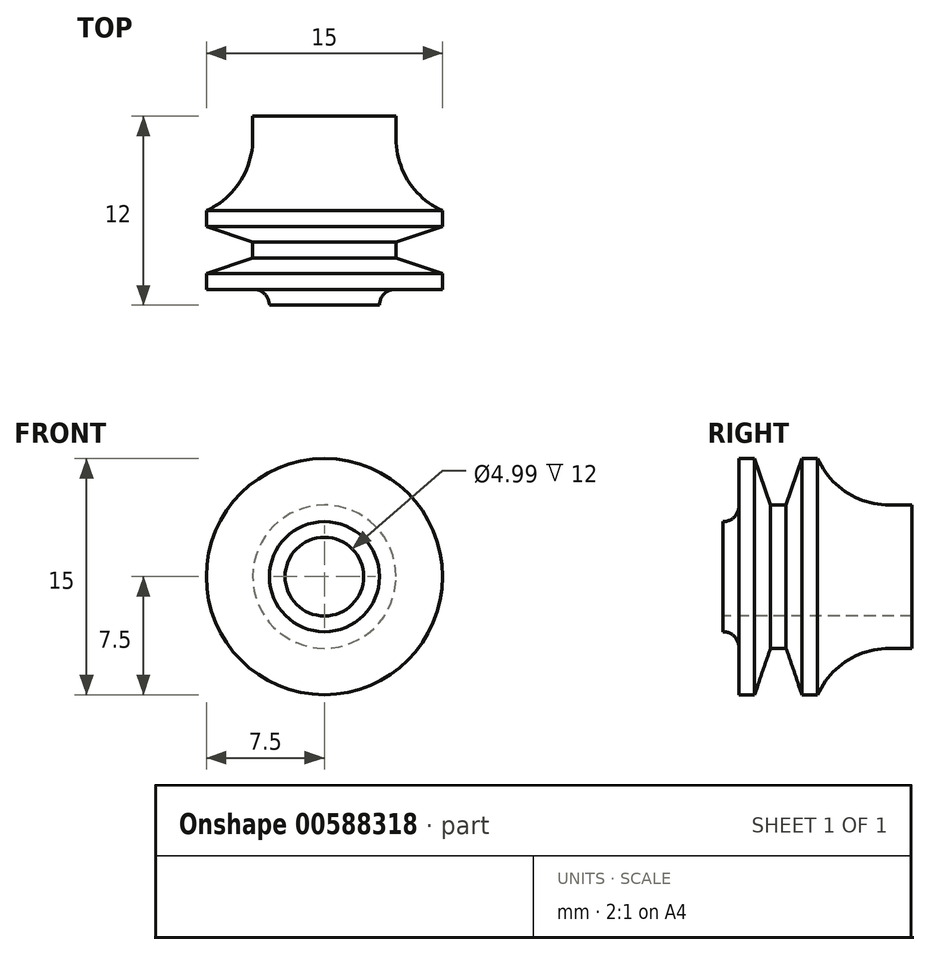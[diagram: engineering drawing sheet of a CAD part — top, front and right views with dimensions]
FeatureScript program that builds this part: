
annotation { "Feature Type Name" : "Feature", "Feature Type Description" : "" }
export const myFeature = defineFeature(function(context is Context, id is Id, definition is map)
    precondition{}
    {
        {
            var Q0;
            Q0=qCreatedBy(makeId("Right.planeOp"),FACE);
            var sketch = newSketch(context, id + "F0", { "sketchPlane" : qUnion([Q0])});
            skLineSegment(sketch, "E0", {"start": v(-124.9, 0) * mm, "end": v(95.35, 0) * mm, "construction": true});
            skLineSegment(sketch, "E1", {"start": v(-35.02, 89.98) * mm, "end": v(-35.02, -71.63) * mm, "construction": true});
            skLineSegment(sketch, "E2", {"start": v(-35.02, 0) * mm, "end": v(-35.02, 5) * mm});
            skLineSegment(sketch, "E3", {"start": v(-35.02, 5) * mm, "end": v(-35.02, 2.5) * mm});
            skLineSegment(sketch, "E4", {"start": v(-35.02, 2.5) * mm, "end": v(-47.02, 2.5) * mm});
            skLineSegment(sketch, "E5", {"start": v(-47.02, 2.5) * mm, "end": v(-47.02, 3.5) * mm});
            skLineSegment(sketch, "E6", {"start": v(-47.02, 3.5) * mm, "end": v(-46.02, 3.5) * mm});
            skLineSegment(sketch, "E7", {"start": v(-35.02, 0) * mm, "end": v(-35.02, 4.55) * mm});
            skLineSegment(sketch, "E8", {"start": v(-35.02, 4.55) * mm, "end": v(-41.02, 4.55) * mm});
            skLineSegment(sketch, "E9", {"start": v(-46.02, 3.5) * mm, "end": v(-46.02, 4.55) * mm});
            skLineSegment(sketch, "E10", {"start": v(-35.02, 0) * mm, "end": v(-35.02, 7.5) * mm});
            skLineSegment(sketch, "E11", {"start": v(-41.02, 7.5) * mm, "end": v(-42.02, 7.5) * mm});
            skLineSegment(sketch, "E12", {"start": v(-46.02, 7.5) * mm, "end": v(-46.02, 4.55) * mm});
            skLineSegment(sketch, "E13", {"start": v(-46.02, 7.5) * mm, "end": v(-45.02, 7.5) * mm});
            skLineSegment(sketch, "E14", {"start": v(-44.02, 4.55) * mm, "end": v(-45.02, 7.5) * mm});
            skLineSegment(sketch, "E15", {"start": v(-44.02, 4.55) * mm, "end": v(-43.52, 4.55) * mm});
            skLineSegment(sketch, "E16", {"start": v(-43.52, 4.55) * mm, "end": v(-43.02, 4.55) * mm});
            skLineSegment(sketch, "E17", {"start": v(-43.02, 4.55) * mm, "end": v(-42.02, 7.5) * mm});
            skLineSegment(sketch, "E18", {"start": v(-42.02, 7.5) * mm, "end": v(-41.02, 7.5) * mm});
            skLineSegment(sketch, "E19", {"start": v(-41.02, 7.5) * mm, "end": v(-41.02, 4.55) * mm});
            skLineSegment(sketch, "E20.trimOffspring", {"start": v(-45.02, 7.5) * mm, "end": v(-46.02, 7.5) * mm});
            skLineSegment(sketch, "E21.trimOffspring", {"start": v(-43.02, 4.55) * mm, "end": v(-44.02, 4.55) * mm});
            skPoint(sketch, "E22.start.orphan", {"position": v(-43.52, 7.5) * mm});
            skSolve(sketch);
        }
        {
            var Q0;
            {var subQ1=sQuery(id+"F0.wireOp",EDGE,"E4");Q0=makeQuery(id+"F0.imprint","IMPRINT",FACE,{"disambiguationData":[TD([[makeQuery(id+"F0.imprint","IMPRINT",EDGE,{"derivedFrom":subQ1}),-1.0]])]});}
            var Q1;
            Q1=sQuery(id+"F0.wireOp",EDGE,"E0");
            revolve(context, id + "F1", {"entities" : qUnion([Q0]), "axis" : qUnion([Q1]), "revolveType" : RevolveType.FULL});
        }
        {
            var Q0;
            Q0=makeQuery(id+"F1.opRevolve","SWEPT_EDGE",EDGE,{"disambiguationData":[OSD([sQuery(id+"F0.wireOp",EDGE,"E8"),sQuery(id+"F0.wireOp",EDGE,"E19")])]});
            fillet(context, id + "F2", {"entities" : qUnion([Q0]), "radius" : 5 * mm, "tangentPropagation" : true, "allowEdgeOverflow" : false});
        }
        {
            var Q0;
            Q0=makeQuery(id+"F1.opRevolve","SWEPT_EDGE",EDGE,{"disambiguationData":[OSD([sQuery(id+"F0.wireOp",EDGE,"E6"),sQuery(id+"F0.wireOp",EDGE,"E9")])]});
            fillet(context, id + "F3", {"entities" : qUnion([Q0]), "radius" : 1 * mm, "tangentPropagation" : true, "allowEdgeOverflow" : false});
        }
    });
